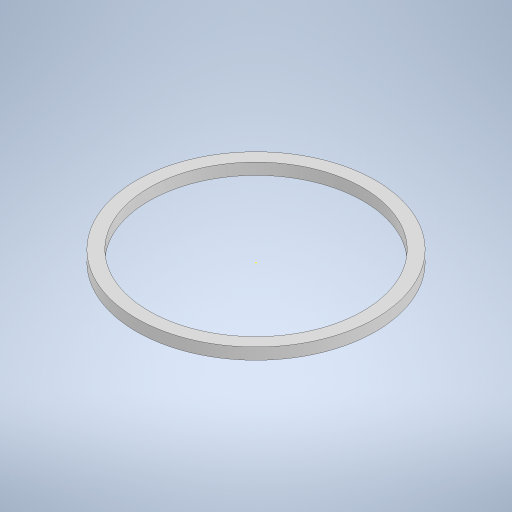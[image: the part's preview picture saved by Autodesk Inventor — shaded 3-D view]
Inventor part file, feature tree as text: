
AUTODESK INVENTOR PART (.ipt)
format: ipt  version: 2023 (Build 270158000, 158)  size: 238,592 bytes
history: native  units: in
note: dims shown in document units (in); Inventor stores cm internally (conversion verified against a paired STEP export)
features: sketch x2, extrude x1
ambient origin geometry x8: Origin, YZ Plane, XZ Plane, XY Plane, X Axis, Y Axis, Z Axis, Center Point
bodies: Solid1 (feature_tree)
feature tree (3):
  sketch  "Sketch1"  dims[d0=9.8425in d1=8.7992in]
  extrude  "Extrusion1"  Depth=8.7992in
  sketch  "Sketch2"  dims[d2=0.4724in d3=0.0in]
